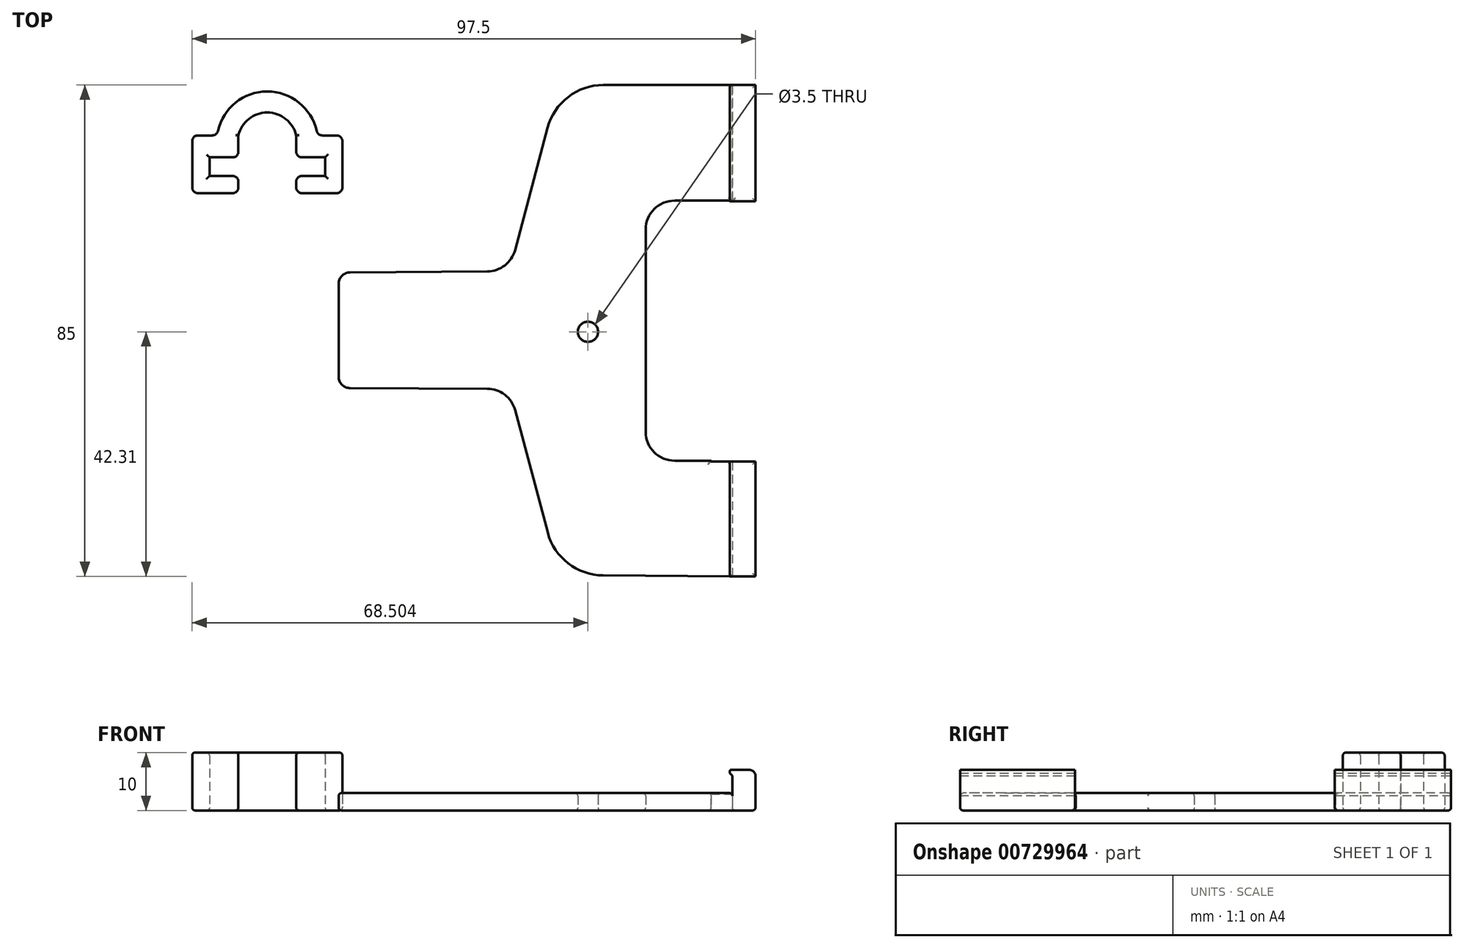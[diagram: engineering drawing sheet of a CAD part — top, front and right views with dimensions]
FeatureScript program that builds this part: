
annotation { "Feature Type Name" : "Feature", "Feature Type Description" : "" }
export const myFeature = defineFeature(function(context is Context, id is Id, definition is map)
    precondition{}
    {
        {
            var Q0;
            Q0=qCreatedBy(makeId("Top.planeOp"),FACE);
            var sketch = newSketch(context, id + "F0", { "sketchPlane" : qUnion([Q0])});
            skLineSegment(sketch, "E0", {"start": v(14.3, 22.7) * mm, "end": v(14.3, -22.3) * mm});
            skLineSegment(sketch, "E1", {"start": v(14.3, -22.3) * mm, "end": v(29.3, -22.3) * mm});
            skLineSegment(sketch, "E2", {"start": v(29.3, -22.3) * mm, "end": v(29.3, -42.3) * mm});
            skLineSegment(sketch, "E3", {"start": v(-38.85, -9.75) * mm, "end": v(-38.85, 10.25) * mm});
            skLineSegment(sketch, "E4", {"start": v(-0.7, 42.7) * mm, "end": v(29.3, 42.7) * mm});
            skLineSegment(sketch, "E5", {"start": v(29.3, 42.7) * mm, "end": v(29.3, 22.7) * mm});
            skLineSegment(sketch, "E6", {"start": v(14.3, 22.7) * mm, "end": v(29.3, 22.7) * mm});
            skCircle(sketch, "E7", {"center": v(4.3, 0) * mm, "radius": 1.75 * mm});
            skLineSegment(sketch, "E8", {"start": v(-0.7, 42.7) * mm, "end": v(-9.3, 10.46) * mm});
            skLineSegment(sketch, "E9.MirrorCS", {"start": v(-0.7, -42.1) * mm, "end": v(-9.3, -9.86) * mm});
            skLineSegment(sketch, "E10", {"start": v(-38.85, 10.25) * mm, "end": v(-9.3, 10.46) * mm});
            skLineSegment(sketch, "E11", {"start": v(-38.85, -9.75) * mm, "end": v(-9.3, -9.86) * mm});
            skLineSegment(sketch, "E12", {"start": v(-0.7, -42.1) * mm, "end": v(29.3, -42.3) * mm});
            skSolve(sketch);
        }
        {
            var Q0;
            Q0=makeQuery(id+"F0.imprint","IMPRINT",FACE,{"disambiguationData":[TD([[makeQuery(id+"F0.imprint","IMPRINT",EDGE,{"derivedFrom":sQuery(id+"F0.wireOp",EDGE,"E0")}),-1.0]])]});
            extrude(context, id + "F1", {"entities" : qUnion([Q0]), "depth" : 3 * mm, "offsetDistance" : 25 * mm});
        }
        {
            var Q0;
            Q0=makeQuery(id+"F1.opExtrude","SWEPT_EDGE",EDGE,{"disambiguationData":[OSD([sQuery(id+"F0.wireOp",EDGE,"E3"),sQuery(id+"F0.wireOp",EDGE,"E11")])]});
            var Q1;
            Q1=makeQuery(id+"F1.opExtrude","SWEPT_EDGE",EDGE,{"disambiguationData":[OSD([sQuery(id+"F0.wireOp",EDGE,"E3"),sQuery(id+"F0.wireOp",EDGE,"E10")])]});
            fillet(context, id + "F2", {"entities" : qUnion([Q0, Q1]), "radius" : 2 * mm, "tangentPropagation" : true, "allowEdgeOverflow" : false});
        }
        {
            var Q0;
            Q0=makeQuery(id+"F1.opExtrude","SWEPT_EDGE",EDGE,{"disambiguationData":[OSD([sQuery(id+"F0.wireOp",EDGE,"E4"),sQuery(id+"F0.wireOp",EDGE,"E8")])]});
            var Q1;
            Q1=makeQuery(id+"F1.opExtrude","SWEPT_EDGE",EDGE,{"disambiguationData":[OSD([sQuery(id+"F0.wireOp",EDGE,"E9.MirrorCS"),sQuery(id+"F0.wireOp",EDGE,"E12")])]});
            fillet(context, id + "F3", {"entities" : qUnion([Q0, Q1]), "radius" : 10 * mm, "tangentPropagation" : true, "allowEdgeOverflow" : false});
        }
        {
            var Q0;
            Q0=makeQuery(id+"F1.opExtrude","SWEPT_EDGE",EDGE,{"disambiguationData":[OSD([sQuery(id+"F0.wireOp",EDGE,"E0"),sQuery(id+"F0.wireOp",EDGE,"E6")])]});
            var Q1;
            Q1=makeQuery(id+"F1.opExtrude","SWEPT_EDGE",EDGE,{"disambiguationData":[OSD([sQuery(id+"F0.wireOp",EDGE,"E0"),sQuery(id+"F0.wireOp",EDGE,"E1")])]});
            var Q2;
            Q2=makeQuery(id+"F1.opExtrude","SWEPT_EDGE",EDGE,{"disambiguationData":[OSD([sQuery(id+"F0.wireOp",EDGE,"E9.MirrorCS"),sQuery(id+"F0.wireOp",EDGE,"E11")])]});
            var Q3;
            Q3=makeQuery(id+"F1.opExtrude","SWEPT_EDGE",EDGE,{"disambiguationData":[OSD([sQuery(id+"F0.wireOp",EDGE,"E8"),sQuery(id+"F0.wireOp",EDGE,"E10")])]});
            fillet(context, id + "F4", {"entities" : qUnion([Q0, Q1, Q2, Q3]), "radius" : 5 * mm, "tangentPropagation" : true, "allowEdgeOverflow" : false});
        }
        {
            var Q0;
            Q0=makeQuery(id+"F1.opExtrude","SWEPT_FACE",FACE,{"disambiguationData":[OSD([sQuery(id+"F0.wireOp",EDGE,"E4")])]});
            var sketch = newSketch(context, id + "F5", { "sketchPlane" : qUnion([Q0])});
            skLineSegment(sketch, "E13", {"start": v(-29.3, 0) * mm, "end": v(-29.3, 6) * mm});
            skLineSegment(sketch, "E14", {"start": v(-33.3, 0) * mm, "end": v(-29.3, 0) * mm});
            skLineSegment(sketch, "E15", {"start": v(-29.3, 6) * mm, "end": v(-28.87, 6.44) * mm});
            skLineSegment(sketch, "E16", {"start": v(-28.87, 6.44) * mm, "end": v(-28.87, 6.8) * mm});
            skLineSegment(sketch, "E17", {"start": v(-29.07, 7) * mm, "end": v(-32.3, 7) * mm});
            skArc(sketch, "E18.filletArc", {"start": v(-28.87, 6.8) * mm, "mid": v(-28.93, 6.94) * mm, "end": v(-29.07, 7) * mm});
            skLineSegment(sketch, "E19", {"start": v(-33.3, 6) * mm, "end": v(-33.3, 0) * mm});
            skArc(sketch, "E20.filletArc", {"start": v(-32.3, 7) * mm, "mid": v(-33.01, 6.7) * mm, "end": v(-33.3, 6) * mm});
            skSolve(sketch);
        }
        {
            var Q0;
            Q0=qCreatedBy(makeId("Top.planeOp"),FACE);
            var sketch = newSketch(context, id + "F6", { "sketchPlane" : qUnion([Q0])});
            skLineSegment(sketch, "E21", {"start": v(-61.2, 30.17) * mm, "end": v(-56.2, 30.17) * mm});
            skLineSegment(sketch, "E22", {"start": v(-41.2, 30.17) * mm, "end": v(-41.2, 26.97) * mm});
            skLineSegment(sketch, "E23", {"start": v(-41.2, 26.97) * mm, "end": v(-46.2, 26.97) * mm});
            skLineSegment(sketch, "E24", {"start": v(-46.2, 26.97) * mm, "end": v(-46.2, 23.97) * mm});
            skLineSegment(sketch, "E25", {"start": v(-46.2, 23.97) * mm, "end": v(-38.2, 23.97) * mm});
            skLineSegment(sketch, "E26", {"start": v(-38.2, 23.97) * mm, "end": v(-38.2, 33.97) * mm});
            skLineSegment(sketch, "E27", {"start": v(-38.2, 33.97) * mm, "end": v(-42.51, 33.97) * mm});
            skLineSegment(sketch, "E28", {"start": v(-64.2, 33.97) * mm, "end": v(-64.2, 23.97) * mm});
            skLineSegment(sketch, "E29", {"start": v(-64.2, 23.97) * mm, "end": v(-56.2, 23.97) * mm});
            skLineSegment(sketch, "E30", {"start": v(-56.2, 23.97) * mm, "end": v(-56.2, 26.97) * mm});
            skLineSegment(sketch, "E31", {"start": v(-56.2, 26.97) * mm, "end": v(-61.2, 26.97) * mm});
            skLineSegment(sketch, "E32", {"start": v(-61.2, 26.97) * mm, "end": v(-61.2, 30.17) * mm});
            skLineSegment(sketch, "E33.trimOffspring", {"start": v(-59.89, 33.97) * mm, "end": v(-64.2, 33.97) * mm});
            skArc(sketch, "E34", {"start": v(-46.2, 33.97) * mm, "mid": v(-51.2, 37.93) * mm, "end": v(-56.2, 33.97) * mm});
            skArc(sketch, "E35", {"start": v(-42.51, 33.97) * mm, "mid": v(-51.2, 41.57) * mm, "end": v(-59.89, 33.97) * mm});
            skLineSegment(sketch, "E36", {"start": v(-56.2, 33.97) * mm, "end": v(-56.2, 30.17) * mm});
            skLineSegment(sketch, "E37", {"start": v(-46.2, 33.97) * mm, "end": v(-46.2, 30.17) * mm});
            skLineSegment(sketch, "E38.trimOffspring", {"start": v(-46.2, 30.17) * mm, "end": v(-41.2, 30.17) * mm});
            skSolve(sketch);
        }
        {
            var Q0;
            Q0=makeQuery(id+"F6.imprint","IMPRINT",FACE,{"disambiguationData":[TD([[makeQuery(id+"F6.imprint","IMPRINT",EDGE,{"derivedFrom":sQuery(id+"F6.wireOp",EDGE,"E21")}),1.0]])]});
            extrude(context, id + "F7", {"entities" : qUnion([Q0]), "depth" : 10 * mm, "offsetDistance" : 25 * mm});
        }
        {
            var Q0;
            Q0=makeQuery(id+"F7.opExtrude","SWEPT_EDGE",EDGE,{"disambiguationData":[OSD([sQuery(id+"F6.wireOp",EDGE,"E28"),sQuery(id+"F6.wireOp",EDGE,"E29")])]});
            var Q1;
            Q1=makeQuery(id+"F7.opExtrude","SWEPT_EDGE",EDGE,{"disambiguationData":[OSD([sQuery(id+"F6.wireOp",EDGE,"E28"),sQuery(id+"F6.wireOp",EDGE,"E33.trimOffspring")])]});
            var Q2;
            Q2=makeQuery(id+"F7.opExtrude","SWEPT_EDGE",EDGE,{"disambiguationData":[OSD([sQuery(id+"F6.wireOp",EDGE,"E33.trimOffspring"),sQuery(id+"F6.wireOp",EDGE,"E35")])]});
            var Q3;
            Q3=makeQuery(id+"F7.opExtrude","SWEPT_EDGE",EDGE,{"disambiguationData":[OSD([sQuery(id+"F6.wireOp",EDGE,"E27"),sQuery(id+"F6.wireOp",EDGE,"E35")])]});
            var Q4;
            Q4=makeQuery(id+"F7.opExtrude","SWEPT_EDGE",EDGE,{"disambiguationData":[OSD([sQuery(id+"F6.wireOp",EDGE,"E26"),sQuery(id+"F6.wireOp",EDGE,"E27")])]});
            var Q5;
            Q5=makeQuery(id+"F7.opExtrude","SWEPT_EDGE",EDGE,{"disambiguationData":[OSD([sQuery(id+"F6.wireOp",EDGE,"E37"),sQuery(id+"F6.wireOp",EDGE,"E38.trimOffspring")])]});
            var Q6;
            Q6=makeQuery(id+"F7.opExtrude","SWEPT_EDGE",EDGE,{"disambiguationData":[OSD([sQuery(id+"F6.wireOp",EDGE,"E21"),sQuery(id+"F6.wireOp",EDGE,"E36")])]});
            var Q7;
            Q7=makeQuery(id+"F7.opExtrude","SWEPT_EDGE",EDGE,{"disambiguationData":[OSD([sQuery(id+"F6.wireOp",EDGE,"E30"),sQuery(id+"F6.wireOp",EDGE,"E31")])]});
            var Q8;
            Q8=makeQuery(id+"F7.opExtrude","SWEPT_EDGE",EDGE,{"disambiguationData":[OSD([sQuery(id+"F6.wireOp",EDGE,"E23"),sQuery(id+"F6.wireOp",EDGE,"E24")])]});
            var Q9;
            Q9=makeQuery(id+"F7.opExtrude","SWEPT_EDGE",EDGE,{"disambiguationData":[OSD([sQuery(id+"F6.wireOp",EDGE,"E25"),sQuery(id+"F6.wireOp",EDGE,"E26")])]});
            var Q10;
            Q10=makeQuery(id+"F7.opExtrude","SWEPT_EDGE",EDGE,{"disambiguationData":[OSD([sQuery(id+"F6.wireOp",EDGE,"E29"),sQuery(id+"F6.wireOp",EDGE,"E30")])]});
            var Q11;
            Q11=makeQuery(id+"F7.opExtrude","SWEPT_EDGE",EDGE,{"disambiguationData":[OSD([sQuery(id+"F6.wireOp",EDGE,"E24"),sQuery(id+"F6.wireOp",EDGE,"E25")])]});
            fillet(context, id + "F8", {"entities" : qUnion([Q0, Q1, Q2, Q3, Q4, Q5, Q6, Q7, Q8, Q9, Q10, Q11]), "radius" : 1 * mm, "tangentPropagation" : true, "allowEdgeOverflow" : false});
        }
        {
            var Q0;
            Q0=makeQuery(id+"F1.opExtrude","CAP_FACE",FACE,{"disambiguationData":[OSD([sQuery(id+"F0.wireOp",EDGE,"E0"),sQuery(id+"F0.wireOp",EDGE,"E1"),sQuery(id+"F0.wireOp",EDGE,"E2"),sQuery(id+"F0.wireOp",EDGE,"E3"),sQuery(id+"F0.wireOp",EDGE,"E4"),sQuery(id+"F0.wireOp",EDGE,"E5"),sQuery(id+"F0.wireOp",EDGE,"E6"),sQuery(id+"F0.wireOp",EDGE,"E7"),sQuery(id+"F0.wireOp",EDGE,"E8"),sQuery(id+"F0.wireOp",EDGE,"E9.MirrorCS"),sQuery(id+"F0.wireOp",EDGE,"E10"),sQuery(id+"F0.wireOp",EDGE,"E11"),sQuery(id+"F0.wireOp",EDGE,"E12")])],"isStart":false});
            var Q1;
            {var subQ0=sQuery(id+"F0.wireOp",EDGE,"E10");var subQ1=sQuery(id+"F0.wireOp",EDGE,"E8");Q1=makeQuery(id+"F4.opFillet","BLEND_EDGE",EDGE,{"blendedFrom":[makeQuery(id+"F1.opExtrude","SWEPT_EDGE",EDGE,{"disambiguationData":[OSD([subQ1,subQ0])]}),makeQuery(id+"F1.opExtrude","CAP_FACE",FACE,{"disambiguationData":[OSD([sQuery(id+"F0.wireOp",EDGE,"E0"),sQuery(id+"F0.wireOp",EDGE,"E1"),sQuery(id+"F0.wireOp",EDGE,"E2"),sQuery(id+"F0.wireOp",EDGE,"E3"),sQuery(id+"F0.wireOp",EDGE,"E4"),sQuery(id+"F0.wireOp",EDGE,"E5"),sQuery(id+"F0.wireOp",EDGE,"E6"),sQuery(id+"F0.wireOp",EDGE,"E7"),subQ1,sQuery(id+"F0.wireOp",EDGE,"E9.MirrorCS"),subQ0,sQuery(id+"F0.wireOp",EDGE,"E11"),sQuery(id+"F0.wireOp",EDGE,"E12")])],"isStart":false})],"blendedInto":[makeQuery(id+"F1.opExtrude","CAP_FACE",FACE,{"disambiguationData":[OSD([sQuery(id+"F0.wireOp",EDGE,"E0"),sQuery(id+"F0.wireOp",EDGE,"E1"),sQuery(id+"F0.wireOp",EDGE,"E2"),sQuery(id+"F0.wireOp",EDGE,"E3"),sQuery(id+"F0.wireOp",EDGE,"E4"),sQuery(id+"F0.wireOp",EDGE,"E5"),sQuery(id+"F0.wireOp",EDGE,"E6"),sQuery(id+"F0.wireOp",EDGE,"E7"),subQ1,sQuery(id+"F0.wireOp",EDGE,"E9.MirrorCS"),subQ0,sQuery(id+"F0.wireOp",EDGE,"E11"),sQuery(id+"F0.wireOp",EDGE,"E12")])],"isStart":false})]});}
            var Q2;
            Q2=makeQuery(id+"F1.opExtrude","CAP_EDGE",EDGE,{"disambiguationData":[OSD([sQuery(id+"F0.wireOp",EDGE,"E10")])],"isStart":false});
            fillet(context, id + "F9", {"entities" : qUnion([Q0, Q1, Q2]), "radius" : 0.5 * mm, "tangentPropagation" : true, "allowEdgeOverflow" : false});
        }
        {
            var Q0;
            {var subQ1=sQuery(id+"F5.wireOp",EDGE,"E14");Q0=makeQuery(id+"F5.imprint","IMPRINT",FACE,{"disambiguationData":[TD([[makeQuery(id+"F5.imprint","IMPRINT",EDGE,{"derivedFrom":subQ1}),1.0]])]});}
            extrude(context, id + "F10", {"entities" : qUnion([Q0]), "operationType" : NewBodyOperationType.ADD, "oppositeDirection" : true, "depth" : 85 * mm, "offsetDistance" : 25 * mm});
        }
        {
            var Q0;
            Q0=makeQuery(id+"F10.opExtrude","SWEPT_FACE",FACE,{"disambiguationData":[OSD([sQuery(id+"F5.wireOp",EDGE,"E19")])]});
            var sketch = newSketch(context, id + "F11", { "sketchPlane" : qUnion([Q0])});
            skLineSegment(sketch, "E39", {"start": v(-22.44, 0) * mm, "end": v(-22.44, 9.74) * mm});
            skLineSegment(sketch, "E40", {"start": v(-22.44, 9.74) * mm, "end": v(22.56, 9.74) * mm});
            skLineSegment(sketch, "E41", {"start": v(22.56, 9.74) * mm, "end": v(22.56, 0) * mm});
            skLineSegment(sketch, "E42", {"start": v(22.56, 0) * mm, "end": v(-22.44, 0) * mm});
            skSolve(sketch);
        }
        {
            var Q0;
            {var subQ0=sQuery(id+"F11.wireOp",EDGE,"E40");Q0=makeQuery(id+"F11.imprint","IMPRINT",FACE,{"disambiguationData":[TD([[makeQuery(id+"F11.imprint","IMPRINT",EDGE,{"derivedFrom":subQ0}),-1.0]])]});}
            var Q1;
            {var subQ0=sQuery(id+"F11.wireOp",EDGE,"E42");Q1=makeQuery(id+"F11.imprint","IMPRINT",FACE,{"disambiguationData":[TD([[makeQuery(id+"F11.imprint","IMPRINT",EDGE,{"derivedFrom":subQ0}),1.0]])]});}
            extrude(context, id + "F12", {"entities" : qUnion([Q0, Q1]), "operationType" : NewBodyOperationType.REMOVE, "oppositeDirection" : true, "depth" : 7.7 * mm, "offsetDistance" : 25 * mm});
        }
        {
            var Q0;
            Q0=makeQuery(id+"F10.boolean.opBoolean","MERGE",FACE,{"derivedFrom":[makeQuery(id+"F1.opExtrude","CAP_FACE",FACE,{"disambiguationData":[OSD([sQuery(id+"F0.wireOp",EDGE,"E0"),sQuery(id+"F0.wireOp",EDGE,"E1"),sQuery(id+"F0.wireOp",EDGE,"E2"),sQuery(id+"F0.wireOp",EDGE,"E3"),sQuery(id+"F0.wireOp",EDGE,"E4"),sQuery(id+"F0.wireOp",EDGE,"E5"),sQuery(id+"F0.wireOp",EDGE,"E6"),sQuery(id+"F0.wireOp",EDGE,"E7"),sQuery(id+"F0.wireOp",EDGE,"E8"),sQuery(id+"F0.wireOp",EDGE,"E9.MirrorCS"),sQuery(id+"F0.wireOp",EDGE,"E10"),sQuery(id+"F0.wireOp",EDGE,"E11"),sQuery(id+"F0.wireOp",EDGE,"E12")])],"isStart":true}),makeQuery(id+"F10.opExtrude","SWEPT_FACE",FACE,{"disambiguationData":[OSD([sQuery(id+"F5.wireOp",EDGE,"E14")])]})]});
            var Q1;
            Q1=makeQuery(id+"F1.opExtrude","CAP_EDGE",EDGE,{"disambiguationData":[OSD([sQuery(id+"F0.wireOp",EDGE,"E11")])],"isStart":true});
            var Q2;
            {var subQ0=sQuery(id+"F0.wireOp",EDGE,"E11");var subQ1=sQuery(id+"F0.wireOp",EDGE,"E9.MirrorCS");Q2=makeQuery(id+"F4.opFillet","BLEND_EDGE",EDGE,{"blendedFrom":[makeQuery(id+"F1.opExtrude","SWEPT_EDGE",EDGE,{"disambiguationData":[OSD([subQ1,subQ0])]}),makeQuery(id+"F1.opExtrude","CAP_FACE",FACE,{"disambiguationData":[OSD([sQuery(id+"F0.wireOp",EDGE,"E0"),sQuery(id+"F0.wireOp",EDGE,"E1"),sQuery(id+"F0.wireOp",EDGE,"E2"),sQuery(id+"F0.wireOp",EDGE,"E3"),sQuery(id+"F0.wireOp",EDGE,"E4"),sQuery(id+"F0.wireOp",EDGE,"E5"),sQuery(id+"F0.wireOp",EDGE,"E6"),sQuery(id+"F0.wireOp",EDGE,"E7"),sQuery(id+"F0.wireOp",EDGE,"E8"),subQ1,sQuery(id+"F0.wireOp",EDGE,"E10"),subQ0,sQuery(id+"F0.wireOp",EDGE,"E12")])],"isStart":true})],"blendedInto":[makeQuery(id+"F1.opExtrude","CAP_FACE",FACE,{"disambiguationData":[OSD([sQuery(id+"F0.wireOp",EDGE,"E0"),sQuery(id+"F0.wireOp",EDGE,"E1"),sQuery(id+"F0.wireOp",EDGE,"E2"),sQuery(id+"F0.wireOp",EDGE,"E3"),sQuery(id+"F0.wireOp",EDGE,"E4"),sQuery(id+"F0.wireOp",EDGE,"E5"),sQuery(id+"F0.wireOp",EDGE,"E6"),sQuery(id+"F0.wireOp",EDGE,"E7"),sQuery(id+"F0.wireOp",EDGE,"E8"),subQ1,sQuery(id+"F0.wireOp",EDGE,"E10"),subQ0,sQuery(id+"F0.wireOp",EDGE,"E12")])],"isStart":true})]});}
            fillet(context, id + "F13", {"entities" : qUnion([Q0, Q1, Q2]), "radius" : 0.5 * mm, "tangentPropagation" : true, "allowEdgeOverflow" : false});
        }
        {
            var Q0;
            Q0=makeQuery(id+"F7.opExtrude","CAP_FACE",FACE,{"disambiguationData":[OSD([sQuery(id+"F6.wireOp",EDGE,"E21"),sQuery(id+"F6.wireOp",EDGE,"E22"),sQuery(id+"F6.wireOp",EDGE,"E23"),sQuery(id+"F6.wireOp",EDGE,"E24"),sQuery(id+"F6.wireOp",EDGE,"E25"),sQuery(id+"F6.wireOp",EDGE,"E26"),sQuery(id+"F6.wireOp",EDGE,"E27"),sQuery(id+"F6.wireOp",EDGE,"E28"),sQuery(id+"F6.wireOp",EDGE,"E29"),sQuery(id+"F6.wireOp",EDGE,"E30"),sQuery(id+"F6.wireOp",EDGE,"E31"),sQuery(id+"F6.wireOp",EDGE,"E32"),sQuery(id+"F6.wireOp",EDGE,"E33.trimOffspring"),sQuery(id+"F6.wireOp",EDGE,"E34"),sQuery(id+"F6.wireOp",EDGE,"E35"),sQuery(id+"F6.wireOp",EDGE,"E36"),sQuery(id+"F6.wireOp",EDGE,"E37"),sQuery(id+"F6.wireOp",EDGE,"E38.trimOffspring")])],"isStart":false});
            var Q1;
            Q1=makeQuery(id+"F7.opExtrude","CAP_FACE",FACE,{"disambiguationData":[OSD([sQuery(id+"F6.wireOp",EDGE,"E21"),sQuery(id+"F6.wireOp",EDGE,"E22"),sQuery(id+"F6.wireOp",EDGE,"E23"),sQuery(id+"F6.wireOp",EDGE,"E24"),sQuery(id+"F6.wireOp",EDGE,"E25"),sQuery(id+"F6.wireOp",EDGE,"E26"),sQuery(id+"F6.wireOp",EDGE,"E27"),sQuery(id+"F6.wireOp",EDGE,"E28"),sQuery(id+"F6.wireOp",EDGE,"E29"),sQuery(id+"F6.wireOp",EDGE,"E30"),sQuery(id+"F6.wireOp",EDGE,"E31"),sQuery(id+"F6.wireOp",EDGE,"E32"),sQuery(id+"F6.wireOp",EDGE,"E33.trimOffspring"),sQuery(id+"F6.wireOp",EDGE,"E34"),sQuery(id+"F6.wireOp",EDGE,"E35"),sQuery(id+"F6.wireOp",EDGE,"E36"),sQuery(id+"F6.wireOp",EDGE,"E37"),sQuery(id+"F6.wireOp",EDGE,"E38.trimOffspring")])],"isStart":true});
            fillet(context, id + "F14", {"entities" : qUnion([Q0, Q1]), "radius" : 0.5 * mm, "tangentPropagation" : true, "allowEdgeOverflow" : false});
        }
    });
